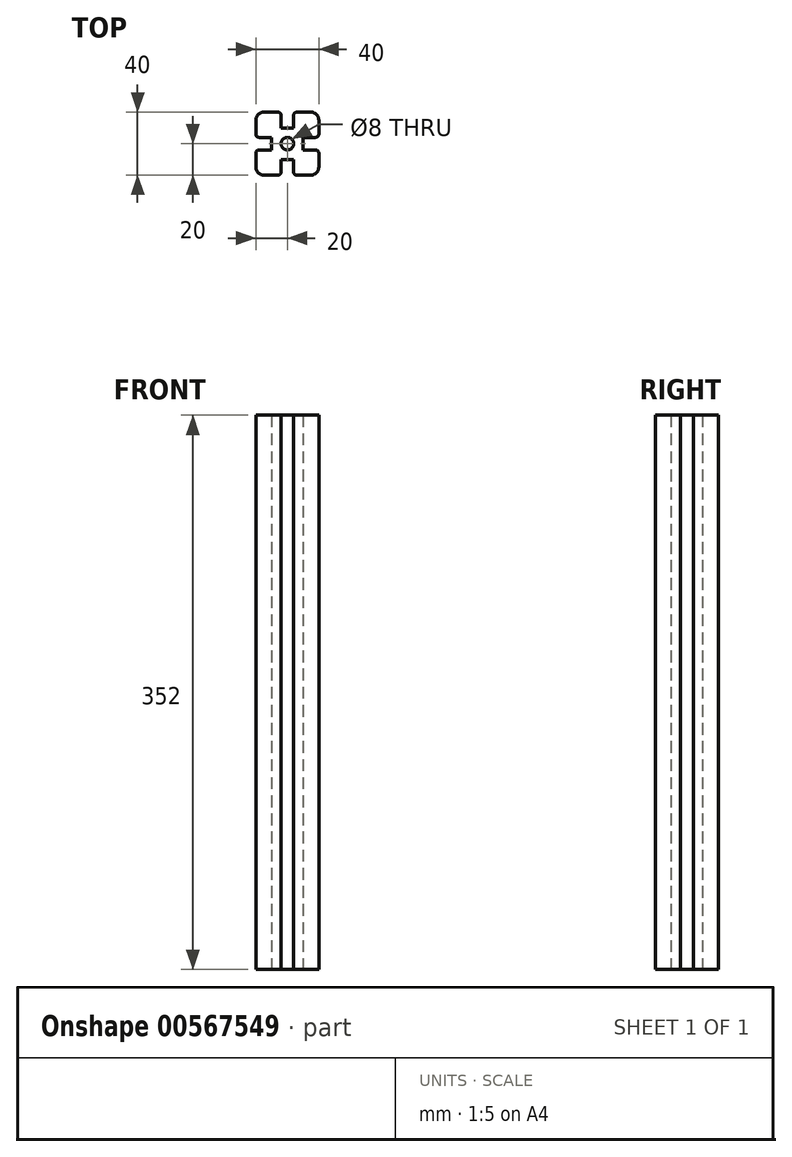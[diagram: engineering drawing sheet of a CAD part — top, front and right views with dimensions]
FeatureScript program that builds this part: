
annotation { "Feature Type Name" : "Feature", "Feature Type Description" : "" }
export const myFeature = defineFeature(function(context is Context, id is Id, definition is map)
    precondition{}
    {
        {
            var Q0;
            Q0=qCreatedBy(makeId("Top.planeOp"),FACE);
            var sketch = newSketch(context, id + "F0", { "sketchPlane" : qUnion([Q0])});
            skLineSegment(sketch, "E0.bottom", {"start": v(20, 20) * mm, "end": v(4, 20) * mm});
            skLineSegment(sketch, "E0.top", {"start": v(20, -20) * mm, "end": v(4, -20) * mm});
            skLineSegment(sketch, "E0.left", {"start": v(20, 20) * mm, "end": v(20, 4) * mm});
            skLineSegment(sketch, "E0.right", {"start": v(-20, 20) * mm, "end": v(-20, 4) * mm});
            skPoint(sketch, "E0.middle", {"position": v(0, 0) * mm});
            skLineSegment(sketch, "E1.bottom", {"start": v(4, 10) * mm, "end": v(-4, 10) * mm});
            skLineSegment(sketch, "E1.left", {"start": v(4, 10) * mm, "end": v(4, 20) * mm});
            skLineSegment(sketch, "E1.right", {"start": v(-4, 10) * mm, "end": v(-4, 20) * mm});
            skPoint(sketch, "E1.middle", {"position": v(0, 20) * mm});
            skLineSegment(sketch, "E2.1.0", {"start": v(-10, -4) * mm, "end": v(-20, -4) * mm});
            skLineSegment(sketch, "E2.1.2", {"start": v(-10, 4) * mm, "end": v(-20, 4) * mm});
            skLineSegment(sketch, "E2.1.3", {"start": v(-10, 4) * mm, "end": v(-10, -4) * mm});
            skLineSegment(sketch, "E2.2.0", {"start": v(4, -10) * mm, "end": v(4, -20) * mm});
            skLineSegment(sketch, "E2.2.1", {"start": v(-4, -30) * mm, "end": v(4, -30) * mm});
            skLineSegment(sketch, "E2.2.2", {"start": v(-4, -10) * mm, "end": v(-4, -20) * mm});
            skLineSegment(sketch, "E2.2.3", {"start": v(-4, -10) * mm, "end": v(4, -10) * mm});
            skLineSegment(sketch, "E2.3.0", {"start": v(10, 4) * mm, "end": v(20, 4) * mm});
            skLineSegment(sketch, "E2.3.2", {"start": v(10, -4) * mm, "end": v(20, -4) * mm});
            skLineSegment(sketch, "E2.3.3", {"start": v(10, -4) * mm, "end": v(10, 4) * mm});
            skLineSegment(sketch, "E3.trimOffspring", {"start": v(20, -4) * mm, "end": v(20, -20) * mm});
            skLineSegment(sketch, "E4.trimOffspring", {"start": v(-4, 20) * mm, "end": v(-20, 20) * mm});
            skPoint(sketch, "E1.top.end.orphan", {"position": v(-4, 30) * mm});
            skPoint(sketch, "E5.orphan", {"position": v(4, 30) * mm});
            skLineSegment(sketch, "E6.trimOffspring", {"start": v(-20, -4) * mm, "end": v(-20, -20) * mm});
            skLineSegment(sketch, "E7.trimOffspring", {"start": v(-4, -20) * mm, "end": v(-20, -20) * mm});
            skCircle(sketch, "E8", {"center": v(0, 0) * mm, "radius": 4 * mm});
            skSolve(sketch);
        }
        {
            var Q0;
            Q0=makeQuery(id+"F0.imprint","IMPRINT",FACE,{"disambiguationData":[TD([[makeQuery(id+"F0.imprint","IMPRINT",EDGE,{"derivedFrom":sQuery(id+"F0.wireOp",EDGE,"E0.bottom")}),1.0]])]});
            extrude(context, id + "F1", {"entities" : qUnion([Q0]), "depth" : 352 * mm, "offsetDistance" : 25 * mm});
        }
        {
            var Q0;
            Q0=makeQuery(id+"F1.opExtrude","SWEPT_EDGE",EDGE,{"disambiguationData":[OSD([sQuery(id+"F0.wireOp",EDGE,"E0.right"),sQuery(id+"F0.wireOp",EDGE,"E4.trimOffspring")])]});
            var Q1;
            Q1=makeQuery(id+"F1.opExtrude","SWEPT_EDGE",EDGE,{"disambiguationData":[OSD([sQuery(id+"F0.wireOp",EDGE,"E6.trimOffspring"),sQuery(id+"F0.wireOp",EDGE,"E7.trimOffspring")])]});
            var Q2;
            Q2=makeQuery(id+"F1.opExtrude","SWEPT_EDGE",EDGE,{"disambiguationData":[OSD([sQuery(id+"F0.wireOp",EDGE,"E0.bottom"),sQuery(id+"F0.wireOp",EDGE,"E0.left")])]});
            var Q3;
            Q3=makeQuery(id+"F1.opExtrude","SWEPT_EDGE",EDGE,{"disambiguationData":[OSD([sQuery(id+"F0.wireOp",EDGE,"E0.top"),sQuery(id+"F0.wireOp",EDGE,"E3.trimOffspring")])]});
            fillet(context, id + "F2", {"entities" : qUnion([Q0, Q1, Q2, Q3]), "radius" : 5 * mm, "tangentPropagation" : true, "allowEdgeOverflow" : false});
        }
        {
            var Q0;
            Q0=makeQuery(id+"F1.opExtrude","SWEPT_EDGE",EDGE,{"disambiguationData":[OSD([sQuery(id+"F0.wireOp",EDGE,"E1.right"),sQuery(id+"F0.wireOp",EDGE,"E4.trimOffspring")])]});
            var Q1;
            Q1=makeQuery(id+"F1.opExtrude","SWEPT_EDGE",EDGE,{"disambiguationData":[OSD([sQuery(id+"F0.wireOp",EDGE,"E0.bottom"),sQuery(id+"F0.wireOp",EDGE,"E1.left")])]});
            var Q2;
            Q2=makeQuery(id+"F1.opExtrude","SWEPT_EDGE",EDGE,{"disambiguationData":[OSD([sQuery(id+"F0.wireOp",EDGE,"E0.left"),sQuery(id+"F0.wireOp",EDGE,"E2.3.0")])]});
            var Q3;
            Q3=makeQuery(id+"F1.opExtrude","SWEPT_EDGE",EDGE,{"disambiguationData":[OSD([sQuery(id+"F0.wireOp",EDGE,"E2.3.2"),sQuery(id+"F0.wireOp",EDGE,"E3.trimOffspring")])]});
            var Q4;
            Q4=makeQuery(id+"F1.opExtrude","SWEPT_EDGE",EDGE,{"disambiguationData":[OSD([sQuery(id+"F0.wireOp",EDGE,"E0.top"),sQuery(id+"F0.wireOp",EDGE,"E2.2.0")])]});
            var Q5;
            Q5=makeQuery(id+"F1.opExtrude","SWEPT_EDGE",EDGE,{"disambiguationData":[OSD([sQuery(id+"F0.wireOp",EDGE,"E2.2.2"),sQuery(id+"F0.wireOp",EDGE,"E7.trimOffspring")])]});
            var Q6;
            Q6=makeQuery(id+"F1.opExtrude","SWEPT_EDGE",EDGE,{"disambiguationData":[OSD([sQuery(id+"F0.wireOp",EDGE,"E2.1.0"),sQuery(id+"F0.wireOp",EDGE,"E6.trimOffspring")])]});
            var Q7;
            Q7=makeQuery(id+"F1.opExtrude","SWEPT_EDGE",EDGE,{"disambiguationData":[OSD([sQuery(id+"F0.wireOp",EDGE,"E0.right"),sQuery(id+"F0.wireOp",EDGE,"E2.1.2")])]});
            fillet(context, id + "F3", {"entities" : qUnion([Q0, Q1, Q2, Q3, Q4, Q5, Q6, Q7]), "radius" : 2 * mm, "tangentPropagation" : true, "allowEdgeOverflow" : false});
        }
    });
